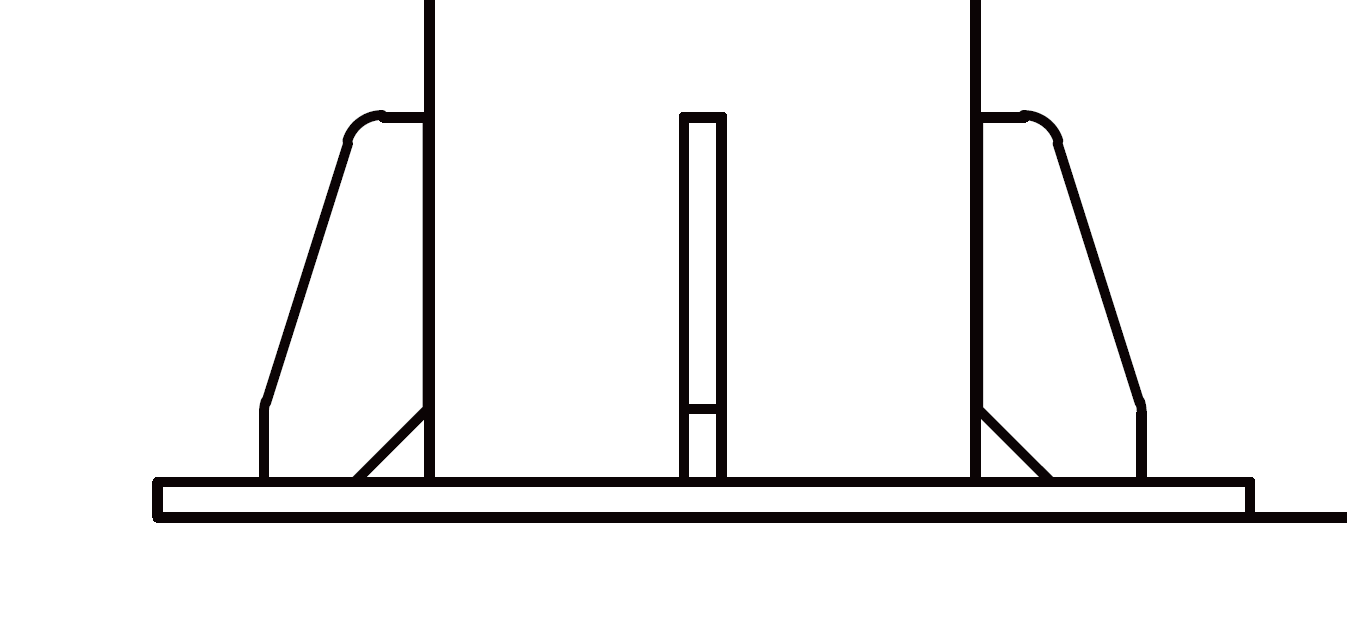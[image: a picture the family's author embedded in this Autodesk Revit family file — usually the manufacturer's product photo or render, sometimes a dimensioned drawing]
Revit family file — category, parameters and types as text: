
# Revit family: Lin1-16.4ft
name_source: partatom
category: Lighting Fixtures
units: mm (PartAtom-declared; Revit-internal decimal feet)

## family parameters
Always vertical = Yes
Cut with Voids When Loaded = No
Light Source = Yes
Maintain Annotation Orientation = No
OmniClass Number = 23.80.70.00
OmniClass Title = Lighting
Part Type = Normal
Room Calculation Point = No
Round Connector Dimension = Use Diameter
Shared = No
Work Plane-Based = No

## types (16) — shared parameters
CRI = 80
Color Filter = 16777215
Default Elevation = 0' - 0"
Dimming Lamp Color Temperature Shift = <None>
H = 16' - 4 13/16"
IP Rating = IP65
Input Voltage = 120-277V
Lamp = LED
Load Classification = Lighting
Manufacturer = Above All Lighting
Power Factor = 0.9
Tilt Angle = 90.00°
URL = https://www.abovealllighting.com

## per-type parameters (varying)
| type | Model | Photometric Web File | Wattage Comments |
| LIN1-30W-3000K-II-16.4ft | LIN1-3030801-II-BK | LIN1-3030801-II-BK.IES | 30W |
| LIN1-30W-3000K-III-16.4ft | LIN1-3030801-III-BK | LIN1-3030801-III-BK.IES | 30W |
| LIN1-30W-3000K-IV-16.4ft | LIN1-3030801-IV-BK | LIN1-3030801-IV-BK.IES | 30W |
| LIN1-30W-3000K-V-16.4ft | LIN1-3030801-V-BK | LIN1-3030801-V-BK.IES | 30W |
| LIN1-40W-3000K-II-16.4ft | LIN1-4030801-II-BK | LIN1-4030801-II-BK.IES | 40W |
| LIN1-40W-3000K-III-16.4ft | LIN1-4030801-III-BK | LIN1-4030801-III-BK.IES | 40W |
| LIN1-40W-3000K-IV-16.4ft | LIN1-4030801-IV-BK | LIN1-4030801-IV-BK.IES | 40W |
| LIN1-40W-3000K-V-16.4ft | LIN1-4030801-V-BK | LIN1-4030801-V-BK.IES | 40W |
| LIN1-50W-3000K-II-16.4ft | LIN1-5030801-II-BK | LIN1-5030801-II-BK.IES | 50W |
| LIN1-50W-3000K-III-16.4ft | LIN1-5030801-III-BK | LIN1-5030801-III-BK.IES | 50W |
| LIN1-50W-3000K-IV-16.4ft | LIN1-5030801-IV-BK | LIN1-6030801-IV-BK.IES | 50W |
| LIN1-50W-3000K-V-16.4ft | LIN1-5030801-V-BK | LIN1-6030801-V-BK.IES | 50W |
| LIN1-60W-3000K-II-16.4ft | LIN1-6030801-II-BK | LIN1-6030801-II-BK.IES | 60W |
| LIN1-60W-3000K-III-16.4ft | LIN1-6030801-III-BK | LIN1-6030801-III-BK.IES | 60W |
| LIN1-60W-3000K-IV-16.4ft | LIN1-6030801-IV-BK | LIN1-6030801-IV-BK.IES | 60W |
| LIN1-60W-3000K-V-16.4ft | LIN1-6030801-V-BK | LIN1-6030801-V-BK.IES | 60W |

## geometry (parser evidence)
native form markers: Sweep x3
no freeform markers — native parametric forms only
